# Revit family: TLS G+D
name_source: partatom
category: Plumbing Fixtures
revit_build: Autodesk Revit 2015 (Build: 20140606_1530(x64)
units: mm (PartAtom-declared; Revit-internal decimal feet)

## types (36) — shared parameters
Aluminium = Aluminum - Polished
Chrome = Chrome - Polished
Glass = Glass
Manufacturer = SanSwiss
Model = TLS G+D
Type Comments = TOP LINE S
URL = http://www.sanswiss.com

## per-type parameters (varying)
| type | A | Aside | B | Bside | C | Cside |
| 1200x900 | 1200 mm | 900 mm | 582 mm | 434 mm | 618 mm | 466 mm  [stored 1.52887 ft] |
| 700x900 | 700 mm | 900 mm | 334 mm | 434 mm | 366 mm | 466 mm  [stored 1.52887 ft] |
| 900x900 | 900 mm | 900 mm | 434 mm | 434 mm | 466 mm  [stored 1.52887 ft] | 466 mm  [stored 1.52887 ft] |
| 900x1000 | 900 mm | 1000 mm  [stored 3.28084 ft] | 434 mm | 484 mm | 466 mm  [stored 1.52887 ft] | 516 mm |
| 750x900 | 750 mm | 900 mm | 359 mm | 434 mm | 391 mm | 466 mm  [stored 1.52887 ft] |
| 800x900 | 800 mm | 900 mm | 384 mm | 434 mm | 416 mm | 466 mm  [stored 1.52887 ft] |
| 1000x900 | 1000 mm  [stored 3.28084 ft] | 900 mm | 484 mm | 434 mm | 516 mm | 466 mm  [stored 1.52887 ft] |
| 700x700 | 700 mm | 700 mm | 334 mm | 334 mm | 366 mm | 366 mm |
| 700x750 | 700 mm | 750 mm | 334 mm | 359 mm | 366 mm | 391 mm |
| 700x800 | 700 mm | 800 mm | 334 mm | 384 mm | 366 mm | 416 mm |
| 700x1000 | 700 mm | 1000 mm  [stored 3.28084 ft] | 334 mm | 484 mm | 366 mm | 516 mm |
| 700x1200 | 700 mm | 1200 mm | 334 mm | 584 mm | 366 mm | 616 mm |
| 750x700 | 750 mm | 700 mm | 359 mm | 334 mm | 391 mm | 366 mm |
| 750x750 | 750 mm | 750 mm | 359 mm | 359 mm | 391 mm | 391 mm |
| 750x800 | 750 mm | 800 mm | 359 mm | 384 mm | 391 mm | 416 mm |
| 750x1000 | 750 mm | 1000 mm  [stored 3.28084 ft] | 359 mm | 484 mm | 391 mm | 516 mm |
| 750x1200 | 750 mm | 1200 mm | 359 mm | 584 mm | 391 mm | 616 mm |
| 800x700 | 800 mm | 700 mm | 384 mm | 334 mm | 416 mm | 366 mm |
| 800x750 | 800 mm | 750 mm | 384 mm | 359 mm | 416 mm | 391 mm |
| 800x800 | 800 mm | 800 mm | 384 mm | 384 mm | 416 mm | 416 mm |
| 800x1000 | 800 mm | 1000 mm  [stored 3.28084 ft] | 384 mm | 484 mm | 416 mm | 516 mm |
| 800x1200 | 800 mm | 1200 mm | 384 mm | 584 mm | 416 mm | 616 mm |
| 900x700 | 900 mm | 700 mm | 434 mm | 334 mm | 466 mm  [stored 1.52887 ft] | 366 mm |
| 900x750 | 900 mm | 750 mm | 434 mm | 359 mm | 466 mm  [stored 1.52887 ft] | 391 mm |
| 900x800 | 900 mm | 800 mm | 434 mm | 384 mm | 466 mm  [stored 1.52887 ft] | 416 mm |
| 900x1200 | 900 mm | 1200 mm | 434 mm | 584 mm | 466 mm  [stored 1.52887 ft] | 616 mm |
| 1000x700 | 1000 mm  [stored 3.28084 ft] | 700 mm | 484 mm | 334 mm | 516 mm | 366 mm |
| 1000x750 | 1000 mm  [stored 3.28084 ft] | 750 mm | 484 mm | 359 mm | 516 mm | 391 mm |
| 1000x800 | 1000 mm  [stored 3.28084 ft] | 800 mm | 484 mm | 384 mm | 516 mm | 416 mm |
| 1000x1200 | 1000 mm  [stored 3.28084 ft] | 1200 mm | 484 mm | 584 mm | 516 mm | 616 mm |
| 1200x700 | 1200 mm | 700 mm | 582 mm | 334 mm | 618 mm | 366 mm |
| 1200x750 | 1200 mm | 750 mm | 582 mm | 359 mm | 618 mm | 391 mm |
| 1200x800 | 1200 mm | 800 mm | 582 mm | 384 mm | 618 mm | 416 mm |
| 1200x1000 | 1200 mm | 1000 mm  [stored 3.28084 ft] | 582 mm | 484 mm | 618 mm | 516 mm |
| 1200x1200 | 1200 mm | 1200 mm | 582 mm | 584 mm | 618 mm | 616 mm |
| 1000x1000 | 1000 mm  [stored 3.28084 ft] | 1000 mm  [stored 3.28084 ft] | 484 mm | 484 mm | 516 mm | 516 mm |

note: [stored X ft] marks values corroborated as IEEE doubles in the binary element streams (Revit-internal decimal feet)

## geometry (parser evidence)
native form markers: Sweep x13
no freeform markers — native parametric forms only
